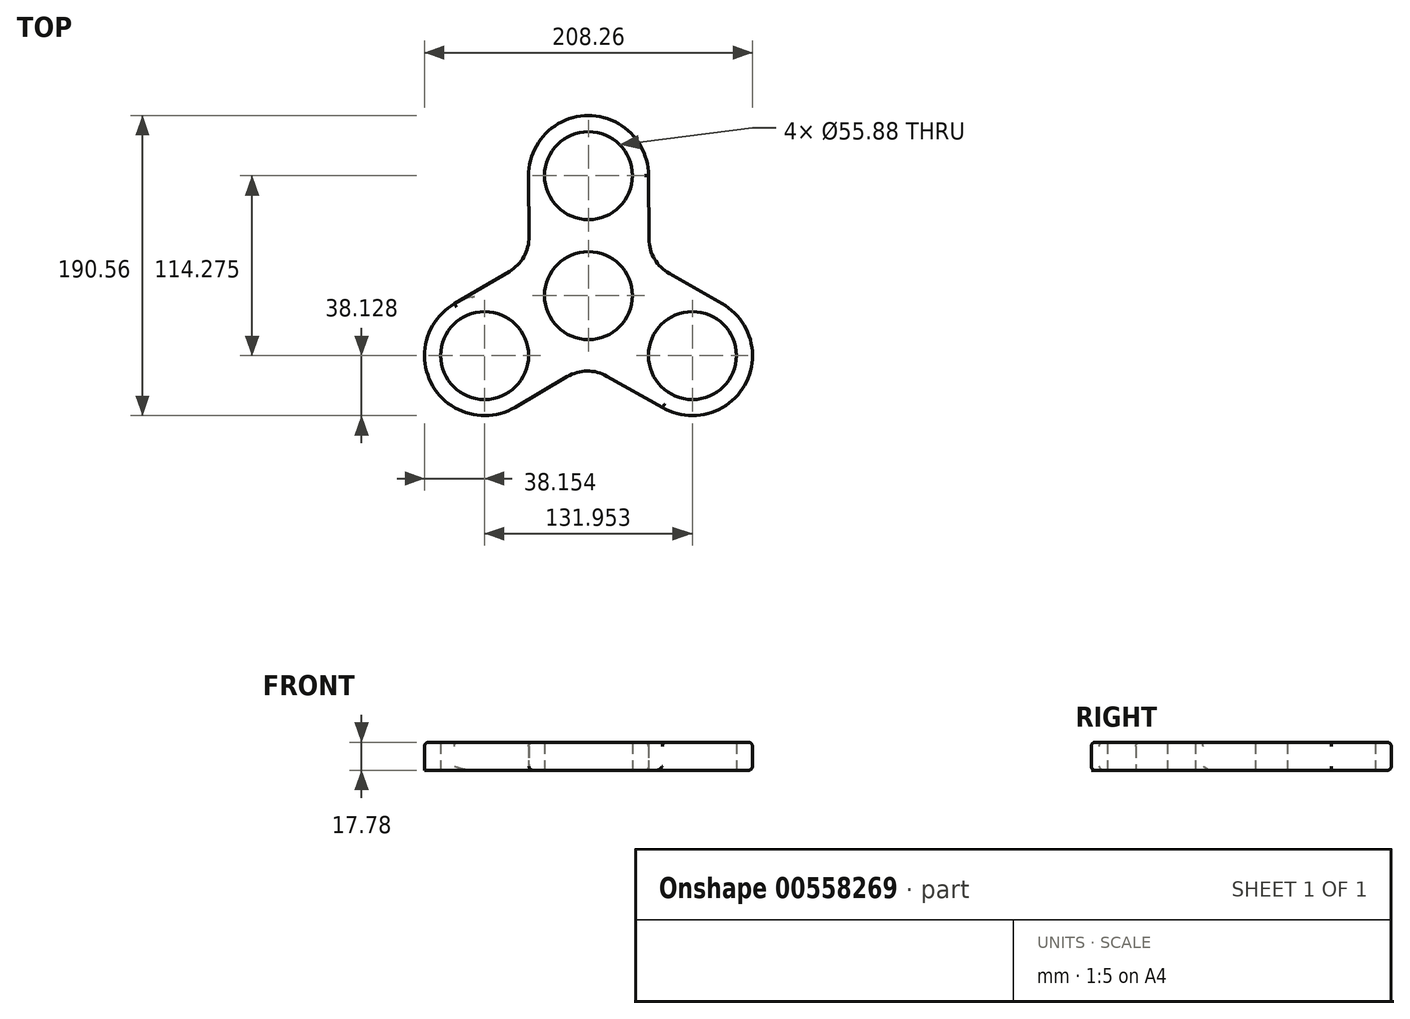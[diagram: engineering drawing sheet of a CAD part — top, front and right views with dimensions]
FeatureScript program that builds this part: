
annotation { "Feature Type Name" : "Feature", "Feature Type Description" : "" }
export const myFeature = defineFeature(function(context is Context, id is Id, definition is map)
    precondition{}
    {
        {
            var Q0;
            Q0=qCreatedBy(makeId("Top.planeOp"),FACE);
            var sketch = newSketch(context, id + "F0", { "sketchPlane" : qUnion([Q0])});
            skCircle(sketch, "E0", {"center": v(0, 0) * mm, "radius": 27.94 * mm});
            skSolve(sketch);
        }
        {
            var Q0;
            Q0=qCreatedBy(makeId("Top.planeOp"),FACE);
            var sketch = newSketch(context, id + "F1", { "sketchPlane" : qUnion([Q0])});
            skCircle(sketch, "E1", {"center": v(0, 76.18) * mm, "radius": 27.94 * mm});
            skCircle(sketch, "E2.1.0", {"center": v(-65.98, -38.1) * mm, "radius": 27.94 * mm});
            skCircle(sketch, "E2.2.0", {"center": v(65.98, -38.1) * mm, "radius": 27.94 * mm});
            skPoint(sketch, "E2.center", {"position": v(0, 0) * mm});
            skSolve(sketch);
        }
        {
            var Q0;
            Q0=makeQuery(id+"F0.imprint","IMPRINT",FACE,{"disambiguationData":[TD([[makeQuery(id+"F0.imprint","IMPRINT",EDGE,{"derivedFrom":sQuery(id+"F0.wireOp",EDGE,"E0")}),1.0]])]});
            extrude(context, id + "F2", {"entities" : qUnion([Q0]), "depth" : 25.4 * mm, "offsetDistance" : 25.4 * mm});
        }
        {
            var Q0;
            Q0=makeQuery(id+"F2.opExtrude","CAP_FACE",FACE,{"disambiguationData":[OSD([sQuery(id+"F0.wireOp",EDGE,"E0")])],"isStart":false});
            extrude(context, id + "F3", {"entities" : qUnion([Q0]), "operationType" : NewBodyOperationType.REMOVE, "oppositeDirection" : true, "depth" : 25.4 * mm, "offsetDistance" : 25.4 * mm});
        }
        {
            var Q0;
            Q0=qCreatedBy(makeId("Top.planeOp"),FACE);
            var sketch = newSketch(context, id + "F4", { "sketchPlane" : qUnion([Q0])});
            skCircle(sketch, "E3", {"center": v(0, 0) * mm, "radius": 27.94 * mm});
            skArc(sketch, "E4", {"start": v(38.1, 76.24) * mm, "mid": v(-0.16, 114.34) * mm, "end": v(-38.1, 75.92) * mm});
            skLineSegment(sketch, "E5", {"start": v(-38.1, 75.92) * mm, "end": v(-37.46, 0) * mm});
            skLineSegment(sketch, "E6", {"start": v(-37.46, 0) * mm, "end": v(0, 0) * mm});
            skLineSegment(sketch, "E7", {"start": v(38.1, 76.24) * mm, "end": v(38.75, 0) * mm});
            skLineSegment(sketch, "E8", {"start": v(38.75, 0) * mm, "end": v(0, 0) * mm});
            skLineSegment(sketch, "E9.1.0", {"start": v(-85.08, -5.13) * mm, "end": v(-19.37, 33.56) * mm});
            skArc(sketch, "E9.1.1", {"start": v(-85.08, -5.13) * mm, "mid": v(-98.94, -57.31) * mm, "end": v(-46.7, -70.96) * mm});
            skLineSegment(sketch, "E9.1.2", {"start": v(-46.7, -70.96) * mm, "end": v(18.73, -32.44) * mm});
            skLineSegment(sketch, "E9.2.0", {"start": v(46.98, -71.12) * mm, "end": v(-19.37, -33.56) * mm});
            skArc(sketch, "E9.2.1", {"start": v(46.98, -71.12) * mm, "mid": v(99.1, -57.03) * mm, "end": v(84.8, -4.97) * mm});
            skLineSegment(sketch, "E9.2.2", {"start": v(84.8, -4.97) * mm, "end": v(18.73, 32.44) * mm});
            skSolve(sketch);
        }
        {
            var Q0;
            {var subQ4=sQuery(id+"F4.wireOp",EDGE,"E9.1.1");Q0=makeQuery(id+"F4.imprint","IMPRINT",FACE,{"disambiguationData":[TD([[makeQuery(id+"F4.imprint","IMPRINT",EDGE,{"derivedFrom":subQ4}),1.0]])]});}
            var Q1;
            {var subQ4=sQuery(id+"F4.wireOp",EDGE,"E4");Q1=makeQuery(id+"F4.imprint","IMPRINT",FACE,{"disambiguationData":[TD([[makeQuery(id+"F4.imprint","IMPRINT",EDGE,{"derivedFrom":subQ4}),1.0]])]});}
            extrude(context, id + "F5", {"entities" : qUnion([Q0, Q1]), "depth" : 17.78 * mm, "offsetDistance" : 25.4 * mm});
        }
        {
            var Q0;
            Q0=makeQuery(id+"F1.imprint","IMPRINT",FACE,{"disambiguationData":[TD([[makeQuery(id+"F1.imprint","IMPRINT",EDGE,{"derivedFrom":sQuery(id+"F1.wireOp",EDGE,"E2.2.0")}),1.0]])]});
            var Q1;
            Q1=makeQuery(id+"F1.imprint","IMPRINT",FACE,{"disambiguationData":[TD([[makeQuery(id+"F1.imprint","IMPRINT",EDGE,{"derivedFrom":sQuery(id+"F1.wireOp",EDGE,"E2.1.0")}),1.0]])]});
            var Q2;
            Q2=makeQuery(id+"F1.imprint","IMPRINT",FACE,{"disambiguationData":[TD([[makeQuery(id+"F1.imprint","IMPRINT",EDGE,{"derivedFrom":sQuery(id+"F1.wireOp",EDGE,"E1")}),1.0]])]});
            extrude(context, id + "F6", {"entities" : qUnion([Q0, Q1, Q2]), "operationType" : NewBodyOperationType.REMOVE, "oppositeDirection" : true, "depth" : -25.4 * mm, "offsetDistance" : 25.4 * mm});
        }
        {
            var Q0;
            Q0=makeQuery(id+"F5.opExtrude","SWEPT_EDGE",EDGE,{"disambiguationData":[OSD([sQuery(id+"F4.wireOp",EDGE,"E9.1.2"),sQuery(id+"F4.wireOp",EDGE,"E9.2.0")])]});
            var Q1;
            Q1=makeQuery(id+"F5.opExtrude","SWEPT_EDGE",EDGE,{"disambiguationData":[OSD([sQuery(id+"F4.wireOp",EDGE,"E5"),sQuery(id+"F4.wireOp",EDGE,"E9.1.0")])]});
            var Q2;
            Q2=makeQuery(id+"F5.opExtrude","SWEPT_EDGE",EDGE,{"disambiguationData":[OSD([sQuery(id+"F4.wireOp",EDGE,"E7"),sQuery(id+"F4.wireOp",EDGE,"E9.2.2")])]});
            fillet(context, id + "F7", {"entities" : qUnion([Q0, Q1, Q2]), "radius" : 25.4 * mm, "tangentPropagation" : true, "allowEdgeOverflow" : false});
        }
        {
            var Q0;
            Q0=makeQuery(id+"F5.opExtrude","CAP_EDGE",EDGE,{"disambiguationData":[OSD([sQuery(id+"F4.wireOp",EDGE,"E7")])],"isStart":false});
            var Q1;
            Q1=makeQuery(id+"F5.opExtrude","CAP_EDGE",EDGE,{"disambiguationData":[OSD([sQuery(id+"F4.wireOp",EDGE,"E4")])],"isStart":false});
            var Q2;
            Q2=makeQuery(id+"F5.opExtrude","CAP_EDGE",EDGE,{"disambiguationData":[OSD([sQuery(id+"F4.wireOp",EDGE,"E9.1.1")])],"isStart":false});
            fillet(context, id + "F8", {"entities" : qUnion([Q0, Q1, Q2]), "radius" : 2.54 * mm, "tangentPropagation" : true, "allowEdgeOverflow" : false});
        }
        {
            var Q0;
            Q0=makeQuery(id+"F5.opExtrude","SWEPT_FACE",FACE,{"disambiguationData":[OSD([sQuery(id+"F4.wireOp",EDGE,"E9.2.1")])]});
            var Q1;
            Q1=makeQuery(id+"F5.opExtrude","CAP_EDGE",EDGE,{"disambiguationData":[OSD([sQuery(id+"F4.wireOp",EDGE,"E4")])],"isStart":true});
            fillet(context, id + "F9", {"entities" : qUnion([Q0, Q1]), "radius" : 2.54 * mm, "tangentPropagation" : true, "allowEdgeOverflow" : false});
        }
    });
